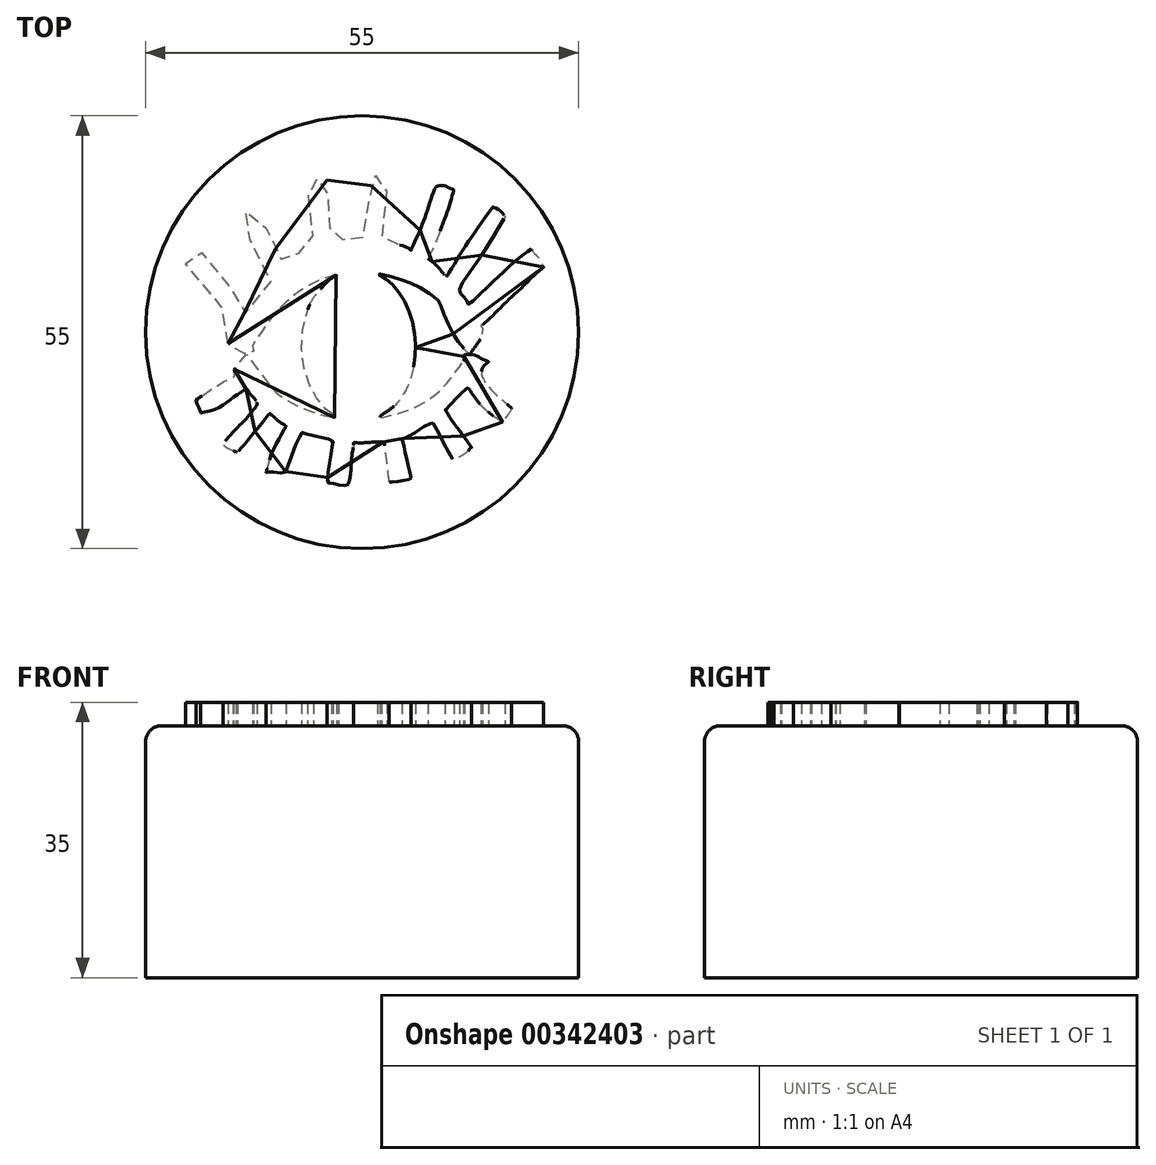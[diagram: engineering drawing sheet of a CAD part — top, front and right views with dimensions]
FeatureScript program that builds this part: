
annotation { "Feature Type Name" : "Feature", "Feature Type Description" : "" }
export const myFeature = defineFeature(function(context is Context, id is Id, definition is map)
    precondition{}
    {
        {
            var Q0;
            Q0=qCreatedBy(makeId("Top.planeOp"),FACE);
            var sketch = newSketch(context, id + "F0", { "sketchPlane" : qUnion([Q0])});
            skSolve(sketch);
        }
        {
            var Q0;
            Q0=qCreatedBy(makeId("Top.planeOp"),FACE);
            var sketch = newSketch(context, id + "F1", { "sketchPlane" : qUnion([Q0])});
            skCircle(sketch, "E0", {"center": v(-27.5, 27.5) * mm, "radius": 27.5 * mm});
            skSolve(sketch);
        }
        {
            var Q0;
            Q0 = qSketchRegion(id + "F1", true);
            extrude(context, id + "F2", {"entities" : qUnion([Q0]), "oppositeDirection" : true, "depth" : 32 * mm});
        }
        {
            var Q0;
            Q0=qCreatedBy(makeId("Top.planeOp"),FACE);
            var sketch = newSketch(context, id + "F3", { "sketchPlane" : qUnion([Q0])});
            skFitSpline(sketch, "E1", {"points": [v(-44.52, 26.06) * mm, v(-43.97, 26.97) * mm, v(-44.23, 28.86) * mm, v(-47.14, 32.93) * mm, v(-49.92, 35.97) * mm, v(-49.75, 36.53) * mm, v(-49.25, 37.45) * mm, v(-48.83, 38.37) * mm, v(-47.26, 36.9) * mm, v(-45.46, 34.82) * mm, v(-44.17, 33) * mm, v(-43.02, 31.05) * mm, v(-42.5, 30.15) * mm, v(-42.38, 29.9) * mm, v(-42.21, 30.03) * mm, v(-40.83, 31.48) * mm, v(-39.13, 33.9) * mm, v(-39.06, 34) * mm, v(-39.2, 34.31) * mm, v(-41.22, 38.18) * mm, v(-42.64, 40.75) * mm, v(-43.35, 41.87) * mm, v(-42.36, 42.77) * mm, v(-40.75, 43.5) * mm, v(-40.34, 42.43) * mm, v(-39.4, 40.2) * mm, v(-38.79, 38.8) * mm, v(-38.25, 37.67) * mm, v(-37.53, 36.27) * mm, v(-37.45, 36.1) * mm, v(-37.18, 36.26) * mm, v(-36.43, 36.72) * mm, v(-35.28, 37.76) * mm, v(-34.25, 38.5) * mm, v(-33.67, 38.77) * mm, v(-33.68, 39.03) * mm, v(-33.77, 40.04) * mm, v(-34.02, 42.42) * mm, v(-34.26, 44.43) * mm, v(-34.41, 46.31) * mm, v(-34.43, 46.83) * mm, v(-34.41, 46.9) * mm, v(-34.3, 46.92) * mm, v(-33.4, 47) * mm, v(-32.39, 46.95) * mm, v(-32.03, 46.88) * mm, v(-31.93, 46.82) * mm, v(-31.95, 46.63) * mm, v(-31.89, 45.07) * mm, v(-31.82, 43.53) * mm, v(-31.7, 41.91) * mm, v(-31.6, 40.66) * mm, v(-31.4, 39.76) * mm, v(-31.4, 39.59) * mm, v(-31.22, 39.5) * mm, v(-30.73, 39.32) * mm, v(-29.75, 39.32) * mm, v(-28.86, 39.43) * mm, v(-27.96, 39.47) * mm, v(-27.47, 39.45) * mm, v(-27.4, 39.44) * mm, v(-27.37, 39.6) * mm, v(-27.11, 40.56) * mm, v(-26.8, 42.42) * mm, v(-26.53, 44.83) * mm, v(-26.24, 46.84) * mm, v(-26.16, 47.19) * mm, v(-26.12, 47.37) * mm, v(-25.88, 47.37) * mm, v(-25.27, 47.35) * mm, v(-24.51, 47.12) * mm, v(-24.37, 47.06) * mm, v(-24.35, 46.79) * mm, v(-24.44, 44.43) * mm, v(-24.73, 41.96) * mm, v(-25.01, 39.56) * mm, v(-25.02, 39.44) * mm, v(-24.93, 39.35) * mm, v(-24.34, 38.99) * mm, v(-23.42, 38.72) * mm, v(-22.64, 38.58) * mm, v(-21.72, 38.24) * mm, v(-21.36, 38) * mm, v(-21.28, 37.93) * mm, v(-21.2, 38.13) * mm, v(-20.17, 40.4) * mm, v(-19.6, 41.84) * mm, v(-19.17, 43.12) * mm, v(-18.8, 44.3) * mm, v(-18.34, 45.5) * mm, v(-18.2, 45.9) * mm, v(-18.18, 46) * mm, v(-17.98, 46.05) * mm, v(-17.36, 46.15) * mm, v(-16.73, 46) * mm, v(-16.38, 45.8) * mm, v(-15.88, 45.63) * mm, v(-15.95, 45.27) * mm, v(-16.34, 43.85) * mm, v(-17.04, 41.81) * mm, v(-18.13, 39) * mm, v(-19.03, 37.03) * mm, v(-19.1, 36.84) * mm, v(-18.88, 36.69) * mm, v(-17.74, 35.64) * mm, v(-16.76, 34.57) * mm, v(-16.61, 34.84) * mm, v(-15.76, 36.22) * mm, v(-14.74, 37.89) * mm, v(-13.43, 39.84) * mm, v(-12.1, 41.77) * mm, v(-10.9, 43.4) * mm, v(-10.88, 43.43) * mm, v(-10.82, 43.4) * mm, v(-10.58, 43.3) * mm, v(-10.14, 43.07) * mm, v(-9.82, 42.8) * mm, v(-9.46, 42.36) * mm, v(-9.4, 42.23) * mm, v(-9.35, 42.13) * mm, v(-9.45, 41.97) * mm, v(-11.5, 38.51) * mm, v(-13.06, 36.22) * mm, v(-15.11, 33) * mm, v(-15.02, 32.48) * mm, v(-14.55, 31.92) * mm, v(-14.1, 31.37) * mm, v(-14.03, 31.07) * mm, v(-12.35, 32.5) * mm, v(-10.63, 34.13) * mm, v(-9.57, 35.14) * mm, v(-8.31, 36.33) * mm, v(-6.54, 37.7) * mm, v(-5.96, 38.06) * mm, v(-5.77, 37.74) * mm, v(-5.06, 36.93) * mm, v(-4.52, 35.98) * mm, v(-4.44, 35.77) * mm, v(-4.86, 35.42) * mm, v(-6.57, 33.8) * mm, v(-8.57, 31.95) * mm, v(-9.6, 30.95) * mm, v(-10.75, 29.76) * mm, v(-12, 28.59) * mm, v(-12.26, 28.41) * mm, v(-12.4, 28.37) * mm, v(-12.29, 28.15) * mm, v(-12.19, 27.95) * mm, v(-12.25, 27.6) * mm, v(-12.38, 26.9) * mm, v(-12.93, 25.96) * mm, v(-13.56, 25.07) * mm, v(-13.72, 24.82) * mm, v(-13.83, 24.75) * mm, v(-14.37, 25.2) * mm, v(-15.45, 26.5) * mm, v(-16.43, 28.3) * mm, v(-17.37, 30.45) * mm, v(-17.71, 31.41) * mm, v(-19.52, 32.79) * mm, v(-21.56, 33.82) * mm, v(-23.69, 34.53) * mm, v(-25.53, 34.95) * mm, v(-24.91, 34.6) * mm, v(-23.69, 33.63) * mm, v(-22.47, 32.05) * mm, v(-21.3, 29.6) * mm, v(-20.8, 26.96) * mm, v(-20.8, 24.27) * mm, v(-21.34, 21.64) * mm, v(-22.3, 19.5) * mm, v(-23.8, 17.81) * mm, v(-25.24, 16.72) * mm, v(-22.97, 17.18) * mm, v(-20.04, 18.35) * mm, v(-17.82, 19.88) * mm, v(-16.47, 21.36) * mm, v(-15.01, 23.3) * mm, v(-14.75, 23.72) * mm, v(-14.58, 24.03) * mm, v(-14.5, 24.3) * mm, v(-14.6, 24.46) * mm, v(-14.55, 24.57) * mm, v(-14.25, 24.66) * mm, v(-13.84, 24.68) * mm, v(-13.03, 24.51) * mm, v(-12.34, 24.17) * mm, v(-11.62, 23.85) * mm, v(-11.41, 23.73) * mm, v(-11.61, 23.59) * mm, v(-12.02, 23.21) * mm, v(-12.34, 22.6) * mm, v(-12.22, 21.8) * mm, v(-11.57, 20.74) * mm, v(-10.43, 19.54) * mm, v(-9.67, 18.86) * mm, v(-9.15, 18.44) * mm, v(-8.7, 18.02) * mm, v(-8.5, 17.82) * mm, v(-8.6, 17.6) * mm, v(-8.83, 17.2) * mm, v(-9.15, 16.77) * mm, v(-9.36, 16.46) * mm, v(-9.53, 16.07) * mm, v(-9.76, 16.15) * mm, v(-10.4, 16.56) * mm, v(-11.33, 17.25) * mm, v(-12.16, 17.98) * mm, v(-12.78, 18.67) * mm, v(-13.09, 19.11) * mm, v(-13.56, 19.74) * mm, v(-13.92, 20.28) * mm, v(-14.03, 20.4) * mm, v(-14.08, 20.47) * mm, v(-14.16, 20.4) * mm, v(-14.83, 19.82) * mm, v(-15.36, 19.31) * mm, v(-15.82, 18.82) * mm, v(-16.13, 18.44) * mm, v(-16.61, 17.96) * mm, v(-16.82, 17.72) * mm, v(-16.94, 17.63) * mm, v(-16.8, 17.4) * mm, v(-16.39, 16.78) * mm, v(-15.92, 16.07) * mm, v(-15.07, 14.9) * mm, v(-14.5, 14.12) * mm, v(-13.94, 13.38) * mm, v(-13.65, 12.99) * mm, v(-13.57, 12.88) * mm, v(-13.7, 12.78) * mm, v(-14.08, 12.4) * mm, v(-14.49, 12.05) * mm, v(-15.12, 11.63) * mm, v(-15.71, 11.38) * mm, v(-15.94, 11.3) * mm, v(-16.2, 11.68) * mm, v(-17.28, 13.73) * mm, v(-17.98, 15.13) * mm, v(-18.4, 15.8) * mm, v(-18.5, 15.97) * mm, v(-18.55, 16.04) * mm, v(-18.7, 15.97) * mm, v(-19.5, 15.56) * mm, v(-20.06, 15.21) * mm, v(-20.62, 14.86) * mm, v(-21.21, 14.49) * mm, v(-21.98, 14.11) * mm, v(-22.28, 14) * mm, v(-22.43, 13.95) * mm, v(-22.37, 13.7) * mm, v(-22.12, 12.67) * mm, v(-21.98, 12.02) * mm, v(-21.82, 11.37) * mm, v(-21.57, 10.3) * mm, v(-21.43, 9.7) * mm, v(-21.29, 8.83) * mm, v(-21.37, 8.82) * mm, v(-21.87, 8.75) * mm, v(-22.5, 8.61) * mm, v(-23.08, 8.5) * mm, v(-23.65, 8.45) * mm, v(-23.93, 8.46) * mm, v(-24.01, 8.48) * mm, v(-24.07, 8.52) * mm, v(-24.07, 8.61) * mm, v(-24.16, 9.55) * mm, v(-24.33, 10.81) * mm, v(-24.45, 11.77) * mm, v(-24.58, 12.62) * mm, v(-24.66, 13.2) * mm, v(-24.72, 13.46) * mm, v(-24.73, 13.53) * mm, v(-24.88, 13.56) * mm, v(-25.68, 13.57) * mm, v(-26.24, 13.53) * mm, v(-26.94, 13.49) * mm, v(-27.52, 13.44) * mm, v(-28.3, 13.46) * mm, v(-28.47, 13.46) * mm, v(-28.58, 13.47) * mm, v(-28.58, 13.35) * mm, v(-28.72, 12.34) * mm, v(-28.83, 11.3) * mm, v(-28.93, 9.91) * mm, v(-29.1, 8.72) * mm, v(-29.19, 8.45) * mm, v(-29.26, 8.15) * mm, v(-29.32, 8.11) * mm, v(-29.6, 8.05) * mm, v(-29.91, 8.03) * mm, v(-30.26, 8.07) * mm, v(-30.6, 8.15) * mm, v(-30.95, 8.23) * mm, v(-31.27, 8.3) * mm, v(-31.48, 8.34) * mm, v(-31.77, 8.33) * mm, v(-31.91, 8.34) * mm, v(-31.93, 8.44) * mm, v(-31.87, 9) * mm, v(-31.79, 9.83) * mm, v(-31.61, 10.98) * mm, v(-31.44, 12) * mm, v(-31.35, 12.6) * mm, v(-31.25, 13.16) * mm, v(-31.2, 13.54) * mm, v(-31.18, 13.6) * mm, v(-31.32, 13.7) * mm, v(-31.79, 13.94) * mm, v(-32.32, 14.08) * mm, v(-33.05, 14.23) * mm, v(-33.9, 14.4) * mm, v(-34.43, 14.54) * mm, v(-34.94, 14.77) * mm, v(-35.08, 14.84) * mm, v(-35.15, 14.7) * mm, v(-35.3, 14.47) * mm, v(-35.55, 14.02) * mm, v(-36.03, 12.97) * mm, v(-36.56, 11.49) * mm, v(-36.95, 10.43) * mm, v(-37.19, 9.83) * mm, v(-37.23, 9.74) * mm, v(-37.38, 9.67) * mm, v(-37.93, 9.62) * mm, v(-38.58, 9.67) * mm, v(-39.15, 9.79) * mm, v(-39.6, 9.71) * mm, v(-39.7, 9.74) * mm, v(-39.49, 10.34) * mm, v(-39.17, 11.63) * mm, v(-38.65, 12.84) * mm, v(-37.95, 14.11) * mm, v(-37.44, 15.04) * mm, v(-37.14, 15.56) * mm, v(-37.34, 15.73) * mm, v(-37.83, 15.98) * mm, v(-38.5, 16.52) * mm, v(-38.9, 16.9) * mm, v(-39.13, 17.1) * mm, v(-39.23, 17.2) * mm, v(-39.38, 17.05) * mm, v(-40.04, 16.19) * mm, v(-40.96, 15.06) * mm, v(-41.55, 14.36) * mm, v(-42.26, 13.4) * mm, v(-42.75, 12.92) * mm, v(-43.31, 12.32) * mm, v(-43.45, 12.3) * mm, v(-43.86, 12.42) * mm, v(-44.48, 12.7) * mm, v(-44.85, 12.92) * mm, v(-45.15, 13.26) * mm, v(-45.04, 13.51) * mm, v(-43.85, 14.86) * mm, v(-42.81, 15.9) * mm, v(-41.95, 16.82) * mm, v(-41.14, 17.86) * mm, v(-40.85, 18.29) * mm, v(-40.85, 18.5) * mm, v(-41.07, 19) * mm, v(-41.55, 19.48) * mm, v(-41.84, 19.78) * mm, v(-42.03, 20.05) * mm, v(-42.16, 20.31) * mm, v(-42.34, 20.27) * mm, v(-42.86, 19.91) * mm, v(-43.54, 19.44) * mm, v(-44.27, 18.88) * mm, v(-45.03, 18.35) * mm, v(-45.86, 17.87) * mm, v(-47, 17.46) * mm, v(-47.9, 17.25) * mm, v(-48, 17.22) * mm, v(-48, 17.34) * mm, v(-48.37, 18.23) * mm, v(-48.6, 18.77) * mm, v(-48.46, 19.01) * mm, v(-47.3, 19.77) * mm, v(-46.48, 20.34) * mm, v(-45.6, 20.93) * mm, v(-44.58, 21.5) * mm, v(-43.77, 21.9) * mm, v(-43.54, 21.95) * mm, v(-43.71, 22.07) * mm, v(-43.74, 22.82) * mm, v(-43.26, 23.52) * mm, v(-42.61, 24.26) * mm, v(-42.32, 24.58) * mm, v(-42.18, 24.72) * mm, v(-42.09, 24.58) * mm, v(-41.68, 23.99) * mm, v(-41.03, 23.1) * mm, v(-40.33, 22.19) * mm, v(-39.43, 21.01) * mm, v(-38.64, 20.07) * mm, v(-38.18, 19.6) * mm, v(-37.25, 19) * mm, v(-36.1, 18.35) * mm, v(-35.13, 17.88) * mm, v(-33.98, 17.44) * mm, v(-32.52, 16.98) * mm, v(-31.65, 16.82) * mm, v(-30.93, 16.69) * mm, v(-30.5, 16.61) * mm, v(-30.7, 16.72) * mm, v(-31.4, 17.1) * mm, v(-32.05, 17.7) * mm, v(-32.97, 18.71) * mm, v(-33.67, 19.77) * mm, v(-34.36, 21.28) * mm, v(-34.98, 23.45) * mm, v(-35.2, 25.78) * mm, v(-34.96, 28.32) * mm, v(-33.98, 31.36) * mm, v(-32.67, 33.1) * mm, v(-31.23, 34.5) * mm, v(-30.75, 34.74) * mm, v(-31.13, 34.7) * mm, v(-32.63, 34.23) * mm, v(-33.79, 33.68) * mm, v(-35.35, 32.77) * mm, v(-36.82, 31.6) * mm, v(-38.38, 30.08) * mm, v(-39.43, 28.83) * mm, v(-40.4, 27.39) * mm, v(-41.42, 25.67) * mm, v(-41.33, 25.07) * mm, v(-42.04, 24.77) * mm, v(-42.62, 24.86) * mm, v(-43.11, 25.15) * mm, v(-43.5, 25.38) * mm, v(-44.12, 25.77) * mm, v(-44.5, 25.97) * mm, v(-44.55, 25.99) * mm, v(-44.52, 26.06) * mm]});
            skSolve(sketch);
        }
        {
            var Q0;
            Q0=makeQuery(id+"F3.imprint","IMPRINT",FACE,{"disambiguationData":[TD([[makeQuery(id+"F3.imprint","IMPRINT",EDGE,{"derivedFrom":sQuery(id+"F3.wireOp",EDGE,"E1")}),-1.0]])]});
            extrude(context, id + "F4", {"entities" : qUnion([Q0]), "operationType" : NewBodyOperationType.ADD, "depth" : 3 * mm});
        }
        {
            var Q0;
            Q0=makeQuery(id+"F2.opExtrude","CAP_EDGE",EDGE,{"disambiguationData":[OSD([sQuery(id+"F1.wireOp",EDGE,"E0")])],"isStart":true});
            fillet(context, id + "F5", {"entities" : qUnion([Q0]), "radius" : 2 * mm, "tangentPropagation" : true, "allowEdgeOverflow" : false});
        }
    });
